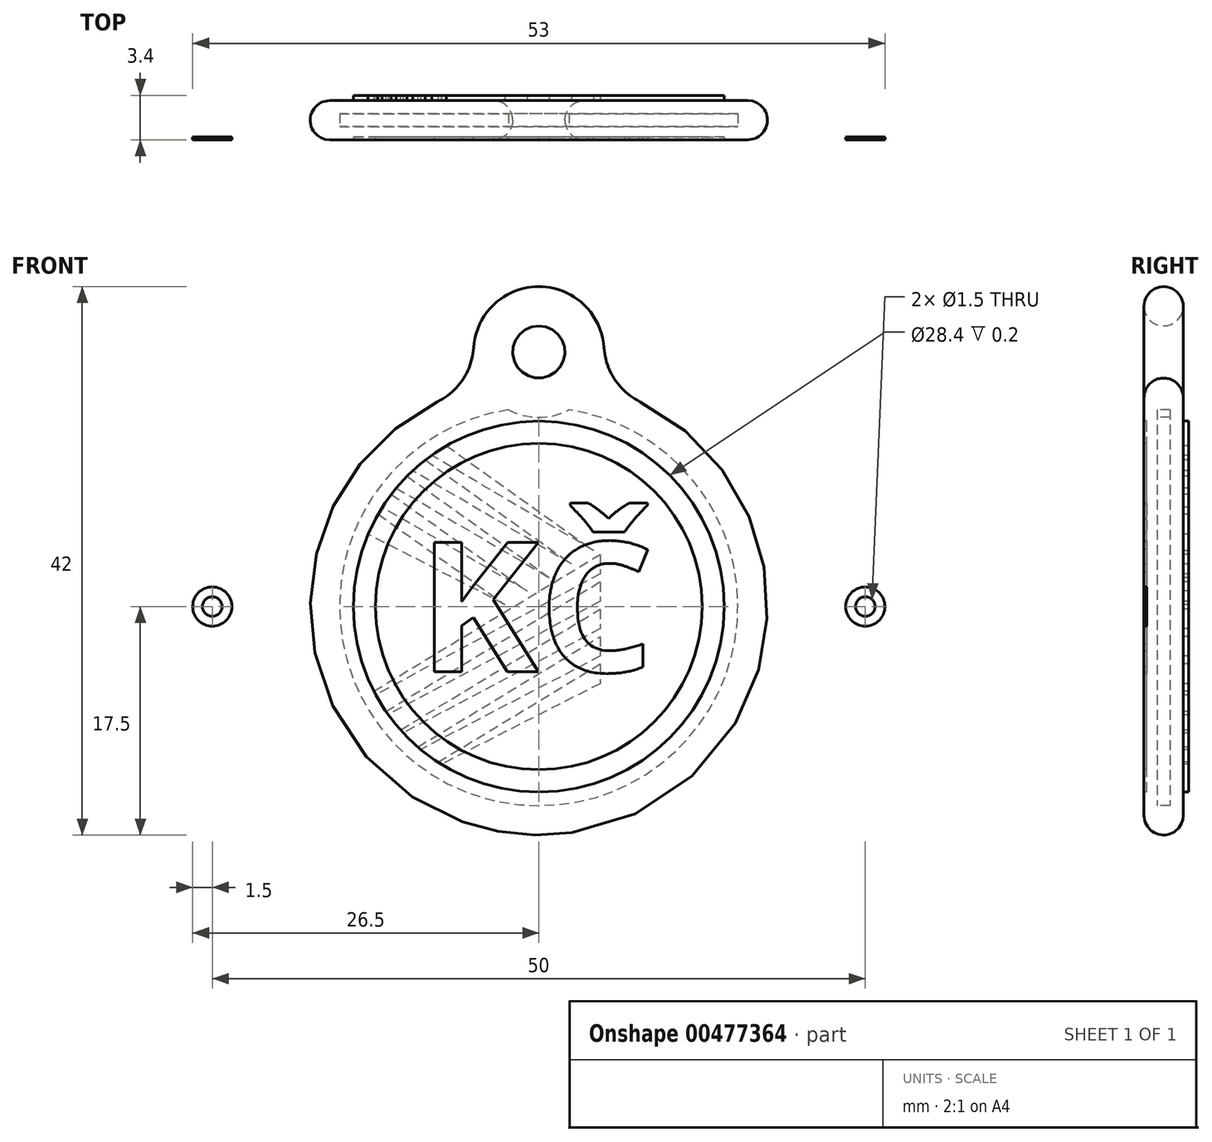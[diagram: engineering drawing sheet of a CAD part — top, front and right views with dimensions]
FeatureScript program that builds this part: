
annotation { "Feature Type Name" : "Feature", "Feature Type Description" : "" }
export const myFeature = defineFeature(function(context is Context, id is Id, definition is map)
    precondition{}
    {
        {
            var Q0;
            Q0=qCreatedBy(makeId("Front.planeOp"),FACE);
            var sketch = newSketch(context, id + "F0", { "sketchPlane" : qUnion([Q0])});
            skCircle(sketch, "E0", {"center": v(0, 0) * mm, "radius": 17.5 * mm});
            skSolve(sketch);
        }
        {
            var Q0;
            Q0=qSketchRegion(id+"F0",true);
            extrude(context, id + "F1", {"entities" : qUnion([Q0]), "depth" : 1 * mm});
        }
        {
            var Q0;
            Q0=makeQuery(id+"F1.opExtrude","CAP_FACE",FACE,{"disambiguationData":[OSD([sQuery(id+"F0.wireOp",EDGE,"E0")])],"isStart":true});
            var sketch = newSketch(context, id + "F2", { "sketchPlane" : qUnion([Q0])});
            skCircle(sketch, "E1", {"center": v(0, 0) * mm, "radius": 17.5 * mm});
            skCircle(sketch, "E2", {"center": v(0, 0) * mm, "radius": 15.25 * mm});
            skSolve(sketch);
        }
        {
            var Q0;
            Q0=qSketchRegion(id+"F2",true);
            extrude(context, id + "F3", {"entities" : qUnion([Q0]), "operationType" : NewBodyOperationType.ADD, "depth" : 1 * mm});
        }
        {
            var Q0;
            Q0=makeQuery(id+"F3.opExtrude","CAP_FACE",FACE,{"disambiguationData":[OSD([sQuery(id+"F2.wireOp",EDGE,"E1"),sQuery(id+"F2.wireOp",EDGE,"E2")])],"isStart":false});
            var sketch = newSketch(context, id + "F4", { "sketchPlane" : qUnion([Q0])});
            skCircle(sketch, "E3", {"center": v(0, 0) * mm, "radius": 17.5 * mm});
            skSolve(sketch);
        }
        {
            var Q0;
            Q0=qSketchRegion(id+"F4",true);
            extrude(context, id + "F5", {"entities" : qUnion([Q0]), "operationType" : NewBodyOperationType.ADD, "depth" : 1 * mm});
        }
        {
            var Q0;
            Q0=makeQuery(id+"F1.opExtrude","CAP_FACE",FACE,{"disambiguationData":[OSD([sQuery(id+"F0.wireOp",EDGE,"E0")])],"isStart":false});
            var sketch = newSketch(context, id + "F6", { "sketchPlane" : qUnion([Q0])});
            skText(sketch, "E4", { "text": "KČ", "fontName": "OpenSans-Bold.ttf"});
            skCircle(sketch, "E5", {"center": v(0, 0) * mm, "radius": 12.5 * mm});
            skCircle(sketch, "E6", {"center": v(0, 0) * mm, "radius": 14.2 * mm});
            const initialGuessF6  = {"E4": [-0.00924, -0.005, 1, 0, 0.01]};
            skSetInitialGuess(sketch, initialGuessF6);
            skSolve(sketch);
        }
        {
            var Q0;
            Q0=makeQuery(id+"F6.imprint","IMPRINT",FACE,{"disambiguationData":[TD([[makeQuery(id+"F6.imprint","IMPRINT",EDGE,{"derivedFrom":sQuery(id+"F6.wireOp",EDGE,"E5")}),-1.0]])]});
            var Q1;
            Q1=makeQuery(id+"F6.imprint","IMPRINT",FACE,{"disambiguationData":[TD([[makeQuery(id+"F6.imprint","IMPRINT",EDGE,{"derivedFrom":sQuery(id+"F6.wireOp",EDGE,"E4.sketch_text.stroke-0")}),-1.0]])]});
            var Q2;
            Q2=makeQuery(id+"F6.imprint","IMPRINT",FACE,{"disambiguationData":[TD([[makeQuery(id+"F6.imprint","IMPRINT",EDGE,{"derivedFrom":sQuery(id+"F6.wireOp",EDGE,"E4.sketch_text.stroke-12")}),-1.0]])]});
            var Q3;
            Q3=makeQuery(id+"F6.imprint","IMPRINT",FACE,{"disambiguationData":[TD([[makeQuery(id+"F6.imprint","IMPRINT",EDGE,{"derivedFrom":sQuery(id+"F6.wireOp",EDGE,"E4.sketch_text.stroke-20")}),-1.0]])]});
            var Q4;
            Q4=makeQuery(id+"F6.imprint","IMPRINT",FACE,{"disambiguationData":[TD([[makeQuery(id+"F6.imprint","IMPRINT",EDGE,{"derivedFrom":sQuery(id+"F6.wireOp",EDGE,"E4.sketch_text.stroke-34")}),-1.0]])]});
            var Q5;
            Q5=makeQuery(id+"F6.imprint","IMPRINT",FACE,{"disambiguationData":[TD([[makeQuery(id+"F6.imprint","IMPRINT",EDGE,{"derivedFrom":sQuery(id+"F6.wireOp",EDGE,"2f791306-b3d7-45ab-86ae-8695a74e6aea.sketch_text.stroke-0")}),-1.0]])]});
            var Q6;
            Q6=makeQuery(id+"F6.imprint","IMPRINT",FACE,{"disambiguationData":[TD([[makeQuery(id+"F6.imprint","IMPRINT",EDGE,{"derivedFrom":sQuery(id+"F6.wireOp",EDGE,"2f791306-b3d7-45ab-86ae-8695a74e6aea.sketch_text.stroke-10")}),-1.0]])]});
            var Q7;
            Q7=makeQuery(id+"F6.imprint","IMPRINT",FACE,{"disambiguationData":[TD([[makeQuery(id+"F6.imprint","IMPRINT",EDGE,{"derivedFrom":sQuery(id+"F6.wireOp",EDGE,"2f791306-b3d7-45ab-86ae-8695a74e6aea.sketch_text.stroke-14")}),-1.0]])]});
            var Q8;
            Q8=makeQuery(id+"F6.imprint","IMPRINT",FACE,{"disambiguationData":[TD([[makeQuery(id+"F6.imprint","IMPRINT",EDGE,{"derivedFrom":sQuery(id+"F6.wireOp",EDGE,"2f791306-b3d7-45ab-86ae-8695a74e6aea.sketch_text.stroke-30")}),-1.0]])]});
            extrude(context, id + "F7", {"entities" : qUnion([Q0, Q1, Q2, Q3, Q4, Q5, Q6, Q7, Q8]), "operationType" : NewBodyOperationType.REMOVE, "oppositeDirection" : true, "depth" : 0.2 * mm});
        }
        {
            var Q0;
            Q0=makeQuery(id+"Fh8yMcBjIkPt4Dr_11.boolean.opBoolean","MERGE",FACE,{"derivedFrom":[makeQuery(id+"F5.opExtrude","CAP_FACE",FACE,{"disambiguationData":[OSD([sQuery(id+"F4.wireOp",EDGE,"E3")])],"isStart":false}),makeQuery(id+"Fh8yMcBjIkPt4Dr_11.opExtrude","CAP_FACE",FACE,{"disambiguationData":[OSD([sQuery(id+"FN8h1bw3wlibMYA_11.wireOp",EDGE,"BS7OUwbq-2ru2-1JD7-GIha-xYvTOZTgPK9A"),sQuery(id+"FN8h1bw3wlibMYA_11.wireOp",EDGE,"aJaIA7Kc-m8c6-AEcG-Va6J-VanrhZFaR41i")])],"isStart":false})]});
            var sketch = newSketch(context, id + "F8", { "sketchPlane" : qUnion([Q0])});
            skArc(sketch, "E7", {"start": v(12.63, -6.5) * mm, "mid": v(14.2, -0.52) * mm, "end": v(13.07, 5.55) * mm});
            skLineSegment(sketch, "E8", {"start": v(12.63, -6.5) * mm, "end": v(-4.7, 4) * mm});
            skLineSegment(sketch, "E9", {"start": v(-4.7, 4) * mm, "end": v(-4.7, 2.5) * mm});
            skLineSegment(sketch, "E10", {"start": v(-4.7, 2.5) * mm, "end": v(12.49, -6.76) * mm});
            skLineSegment(sketch, "E11", {"start": v(-4.7, 1.9) * mm, "end": v(-4.7, 0.4) * mm});
            skLineSegment(sketch, "E12", {"start": v(-4.7, 0.4) * mm, "end": v(11.53, -8.28) * mm});
            skLineSegment(sketch, "E13", {"start": v(11.7, -8.04) * mm, "end": v(-4.7, 1.9) * mm});
            skLineSegment(sketch, "E14", {"start": v(-4.7, -0.2) * mm, "end": v(-4.7, -1.7) * mm});
            skLineSegment(sketch, "E15", {"start": v(-4.7, -1.7) * mm, "end": v(10.39, -9.68) * mm});
            skLineSegment(sketch, "E16", {"start": v(10.6, -9.46) * mm, "end": v(-4.7, -0.2) * mm});
            skLineSegment(sketch, "E17", {"start": v(-4.7, -2.3) * mm, "end": v(-4.7, -3.8) * mm});
            skLineSegment(sketch, "E18", {"start": v(-4.7, -3.8) * mm, "end": v(9.04, -10.95) * mm});
            skLineSegment(sketch, "E19", {"start": v(9.27, -10.76) * mm, "end": v(-4.7, -2.3) * mm});
            skLineSegment(sketch, "E20", {"start": v(-4.7, -4.4) * mm, "end": v(-4.7, -5.9) * mm});
            skLineSegment(sketch, "E21", {"start": v(-4.7, -5.9) * mm, "end": v(7.46, -12.08) * mm});
            skLineSegment(sketch, "E22", {"start": v(7.72, -11.92) * mm, "end": v(-4.7, -4.4) * mm});
            skArc(sketch, "E23.trimOffspring", {"start": v(11.7, -8.04) * mm, "mid": v(12.11, -7.4) * mm, "end": v(12.49, -6.76) * mm});
            skArc(sketch, "E24.trimOffspring", {"start": v(10.6, -9.46) * mm, "mid": v(11.08, -8.88) * mm, "end": v(11.53, -8.28) * mm});
            skArc(sketch, "E25.trimOffspring", {"start": v(9.27, -10.76) * mm, "mid": v(9.84, -10.24) * mm, "end": v(10.39, -9.68) * mm});
            skArc(sketch, "E26.trimOffspring", {"start": v(7.72, -11.92) * mm, "mid": v(8.4, -11.46) * mm, "end": v(9.04, -10.95) * mm});
            skLineSegment(sketch, "E27", {"start": v(7.07, 12.32) * mm, "end": v(-4.2, 4.28) * mm});
            skLineSegment(sketch, "E28", {"start": v(-4.2, 4.28) * mm, "end": v(8.2, 11.59) * mm});
            skLineSegment(sketch, "E29", {"start": v(8.69, 11.23) * mm, "end": v(-2.5, 3.25) * mm});
            skLineSegment(sketch, "E30", {"start": v(-2.5, 3.25) * mm, "end": v(9.66, 10.4) * mm});
            skLineSegment(sketch, "E31", {"start": v(10.1, 10) * mm, "end": v(-0.8, 2.22) * mm});
            skLineSegment(sketch, "E32", {"start": v(11.3, 8.6) * mm, "end": v(0.9, 1.2) * mm});
            skLineSegment(sketch, "E33", {"start": v(0.9, 1.2) * mm, "end": v(12, 7.6) * mm});
            skLineSegment(sketch, "E34", {"start": v(12.3, 7.09) * mm, "end": v(2.6, 0.16) * mm});
            skLineSegment(sketch, "E35", {"start": v(2.6, 0.16) * mm, "end": v(13.07, 5.55) * mm});
            skArc(sketch, "E36.trimOffspring", {"start": v(7.07, 12.32) * mm, "mid": v(-14.2, -0.23) * mm, "end": v(7.46, -12.08) * mm});
            skArc(sketch, "E37.trimOffspring", {"start": v(8.69, 11.23) * mm, "mid": v(8.45, 11.41) * mm, "end": v(8.2, 11.59) * mm});
            skArc(sketch, "E38.trimOffspring", {"start": v(10.1, 10) * mm, "mid": v(9.88, 10.2) * mm, "end": v(9.66, 10.4) * mm});
            skArc(sketch, "E39.trimOffspring", {"start": v(11.3, 8.6) * mm, "mid": v(11.1, 8.84) * mm, "end": v(10.92, 9.08) * mm});
            skArc(sketch, "E40.trimOffspring", {"start": v(12.3, 7.09) * mm, "mid": v(12.15, 7.34) * mm, "end": v(12, 7.6) * mm});
            skLineSegment(sketch, "E41", {"start": v(10.92, 9.08) * mm, "end": v(-0.8, 2.22) * mm});
            skSolve(sketch);
        }
        {
            var Q0;
            Q0=qSketchRegion(id+"F8",true);
            extrude(context, id + "F9", {"entities" : qUnion([Q0]), "operationType" : NewBodyOperationType.ADD, "depth" : 0.4 * mm});
        }
        {
            var Q0;
            {var subQ0=sQuery(id+"F0.wireOp",EDGE,"E0");Q0=makeQuery(id+"F7.boolean.opBoolean","SPLIT",FACE,{"disambiguationData":[TD([makeQuery(id+"F1.opExtrude","SWEPT_FACE",FACE,{"disambiguationData":[OSD([subQ0])]})])],"derivedFrom":makeQuery(id+"F1.opExtrude","CAP_FACE",FACE,{"disambiguationData":[OSD([subQ0])],"isStart":false})});}
            var sketch = newSketch(context, id + "F10", { "sketchPlane" : qUnion([Q0])});
            skCircle(sketch, "E42", {"center": v(0, 19.5) * mm, "radius": 2 * mm});
            skCircle(sketch, "E43", {"center": v(0, 19.5) * mm, "radius": 5 * mm});
            skSolve(sketch);
        }
        {
            var Q0;
            Q0=qSketchRegion(id+"F10",true);
            var Q1;
            Q1=makeQuery(id+"F5.opExtrude","CAP_FACE",FACE,{"disambiguationData":[OSD([sQuery(id+"F4.wireOp",EDGE,"E3")])],"isStart":false});
            extrude(context, id + "F11", {"entities" : qUnion([Q0]), "operationType" : NewBodyOperationType.ADD, "endBound" : BoundingType.UP_TO_SURFACE, "oppositeDirection" : true, "endBoundEntityFace" : qUnion([Q1]), "depth" : 25 * mm});
        }
        {
            var Q0;
            Q0=makeQuery(id+"F11.boolean.opBoolean","INTERSECT",EDGE,{"disambiguationData":[OD(0.0)],"derivedFrom":[makeQuery(id+"F5.boolean.opBoolean","MERGE",FACE,{"derivedFrom":[makeQuery(id+"F3.boolean.opBoolean","MERGE",FACE,{"derivedFrom":[makeQuery(id+"F1.opExtrude","SWEPT_FACE",FACE,{"disambiguationData":[OSD([sQuery(id+"F0.wireOp",EDGE,"E0")])]}),makeQuery(id+"F3.opExtrude","SWEPT_FACE",FACE,{"disambiguationData":[OSD([sQuery(id+"F2.wireOp",EDGE,"E1")])]})]}),makeQuery(id+"F5.opExtrude","SWEPT_FACE",FACE,{"disambiguationData":[OSD([sQuery(id+"F4.wireOp",EDGE,"E3")])]})]}),makeQuery(id+"F11.opExtrude","SWEPT_FACE",FACE,{"disambiguationData":[OSD([sQuery(id+"F10.wireOp",EDGE,"E43")])]})]});
            var Q1;
            Q1=makeQuery(id+"F11.boolean.opBoolean","INTERSECT",EDGE,{"disambiguationData":[OD(1.0)],"derivedFrom":[makeQuery(id+"F5.boolean.opBoolean","MERGE",FACE,{"derivedFrom":[makeQuery(id+"F3.boolean.opBoolean","MERGE",FACE,{"derivedFrom":[makeQuery(id+"F1.opExtrude","SWEPT_FACE",FACE,{"disambiguationData":[OSD([sQuery(id+"F0.wireOp",EDGE,"E0")])]}),makeQuery(id+"F3.opExtrude","SWEPT_FACE",FACE,{"disambiguationData":[OSD([sQuery(id+"F2.wireOp",EDGE,"E1")])]})]}),makeQuery(id+"F5.opExtrude","SWEPT_FACE",FACE,{"disambiguationData":[OSD([sQuery(id+"F4.wireOp",EDGE,"E3")])]})]}),makeQuery(id+"F11.opExtrude","SWEPT_FACE",FACE,{"disambiguationData":[OSD([sQuery(id+"F10.wireOp",EDGE,"E43")])]})]});
            fillet(context, id + "F12", {"entities" : qUnion([Q0, Q1]), "radius" : 5 * mm, "tangentPropagation" : true, "allowEdgeOverflow" : false});
        }
        {
            var Q0;
            Q0=makeQuery(id+"F1.opExtrude","CAP_EDGE",EDGE,{"disambiguationData":[OSD([sQuery(id+"F0.wireOp",EDGE,"E0")])],"isStart":false});
            var Q1;
            {var subQ0=sQuery(id+"F10.wireOp",EDGE,"E43");var subQ1=sQuery(id+"F4.wireOp",EDGE,"E3");Q1=makeQuery(id+"F12.opFillet","BLEND_EDGE",EDGE,{"blendedFrom":[makeQuery(id+"F11.boolean.opBoolean","INTERSECT",EDGE,{"disambiguationData":[OD(0.0)],"derivedFrom":[makeQuery(id+"F5.boolean.opBoolean","MERGE",FACE,{"derivedFrom":[makeQuery(id+"F3.boolean.opBoolean","MERGE",FACE,{"derivedFrom":[makeQuery(id+"F1.opExtrude","SWEPT_FACE",FACE,{"disambiguationData":[OSD([sQuery(id+"F0.wireOp",EDGE,"E0")])]}),makeQuery(id+"F3.opExtrude","SWEPT_FACE",FACE,{"disambiguationData":[OSD([sQuery(id+"F2.wireOp",EDGE,"E1")])]})]}),makeQuery(id+"F5.opExtrude","SWEPT_FACE",FACE,{"disambiguationData":[OSD([subQ1])]})]}),makeQuery(id+"F11.opExtrude","SWEPT_FACE",FACE,{"disambiguationData":[OSD([subQ0])]})]}),makeQuery(id+"F11.boolean.opBoolean","MERGE",FACE,{"derivedFrom":[makeQuery(id+"F5.opExtrude","CAP_FACE",FACE,{"disambiguationData":[OSD([subQ1])],"isStart":false}),makeQuery(id+"F11.opExtrude","CAP_FACE",FACE,{"disambiguationData":[OSD([sQuery(id+"F10.wireOp",EDGE,"E42"),subQ0])],"isStart":false})]})],"blendedInto":[makeQuery(id+"F11.boolean.opBoolean","MERGE",FACE,{"derivedFrom":[makeQuery(id+"F5.opExtrude","CAP_FACE",FACE,{"disambiguationData":[OSD([subQ1])],"isStart":false}),makeQuery(id+"F11.opExtrude","CAP_FACE",FACE,{"disambiguationData":[OSD([sQuery(id+"F10.wireOp",EDGE,"E42"),subQ0])],"isStart":false})]})]});}
            var Q2;
            Q2=makeQuery(id+"F11.opExtrude","CAP_EDGE",EDGE,{"disambiguationData":[OSD([sQuery(id+"F10.wireOp",EDGE,"E42")])],"isStart":true});
            var Q3;
            Q3=makeQuery(id+"F11.opExtrude","CAP_EDGE",EDGE,{"disambiguationData":[OSD([sQuery(id+"F10.wireOp",EDGE,"E42")])],"isStart":false});
            fillet(context, id + "F13", {"entities" : qUnion([Q0, Q1, Q2, Q3]), "radius" : 1.5 * mm, "tangentPropagation" : true, "allowEdgeOverflow" : false});
        }
        {
            var Q0;
            {var subQ0=sQuery(id+"F0.wireOp",EDGE,"E0");Q0=makeQuery(id+"F11.boolean.opBoolean","MERGE",FACE,{"derivedFrom":[makeQuery(id+"F7.boolean.opBoolean","SPLIT",FACE,{"disambiguationData":[TD([makeQuery(id+"F1.opExtrude","SWEPT_FACE",FACE,{"disambiguationData":[OSD([subQ0])]})])],"derivedFrom":makeQuery(id+"F1.opExtrude","CAP_FACE",FACE,{"disambiguationData":[OSD([subQ0])],"isStart":false})}),makeQuery(id+"F11.opExtrude","CAP_FACE",FACE,{"disambiguationData":[OSD([sQuery(id+"F10.wireOp",EDGE,"E42"),sQuery(id+"F10.wireOp",EDGE,"E43")])],"isStart":true})]});}
            var sketch = newSketch(context, id + "F14", { "sketchPlane" : qUnion([Q0])});
            skCircle(sketch, "E44", {"center": v(-25, 0) * mm, "radius": 1.5 * mm});
            skCircle(sketch, "E45", {"center": v(25, 0) * mm, "radius": 1.5 * mm});
            skCircle(sketch, "E46", {"center": v(25, 0) * mm, "radius": 0.75 * mm});
            skCircle(sketch, "E47", {"center": v(-25, 0) * mm, "radius": 0.75 * mm});
            skSolve(sketch);
        }
        {
            var Q0;
            Q0=qSketchRegion(id+"F14",true);
            extrude(context, id + "F15", {"entities" : qUnion([Q0]), "oppositeDirection" : true, "depth" : 0.2 * mm});
        }
    });
